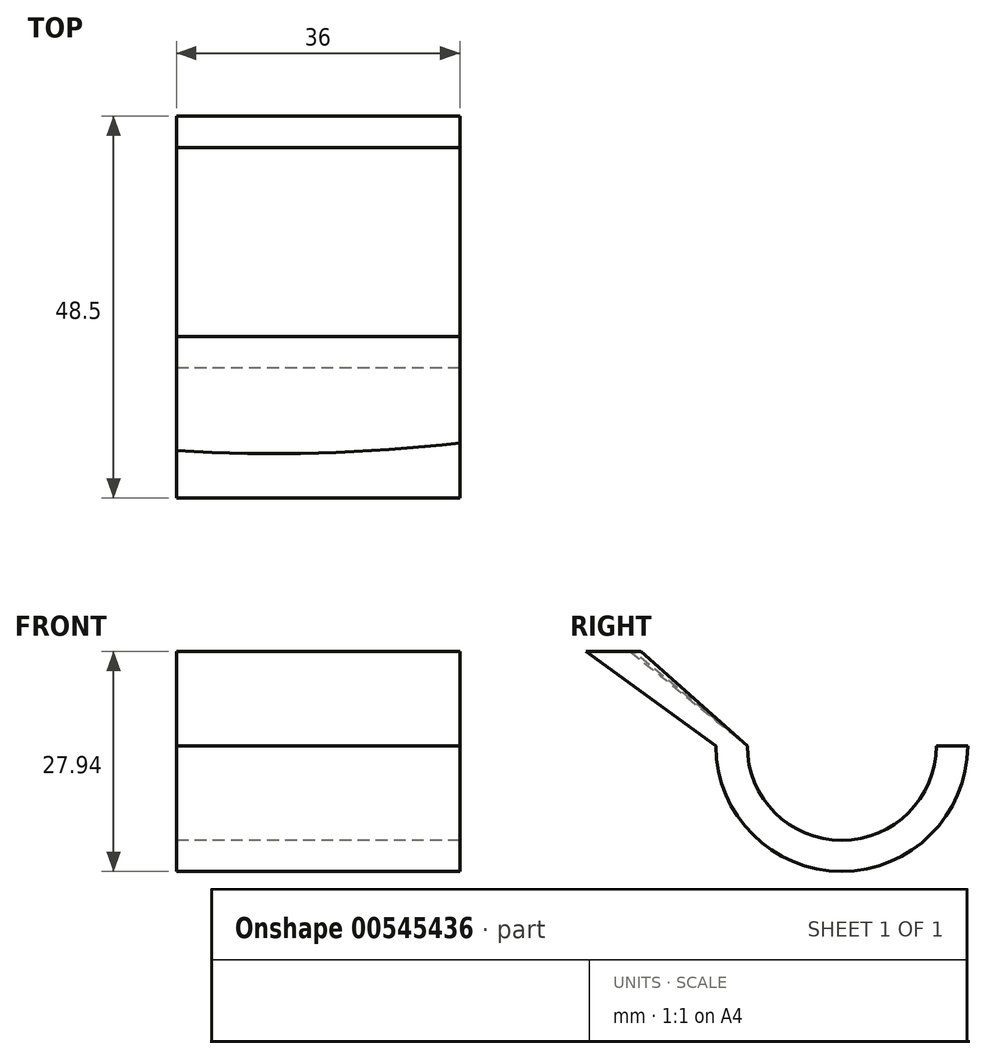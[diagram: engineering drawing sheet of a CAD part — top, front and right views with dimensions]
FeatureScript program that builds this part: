
annotation { "Feature Type Name" : "Feature", "Feature Type Description" : "" }
export const myFeature = defineFeature(function(context is Context, id is Id, definition is map)
    precondition{}
    {
        {
            var Q0;
            Q0=qCreatedBy(makeId("Right.planeOp"),FACE);
            var sketch = newSketch(context, id + "F0", { "sketchPlane" : qUnion([Q0])});
            skArc(sketch, "E0", {"start": v(-12, 0) * mm, "mid": v(0, -12) * mm, "end": v(12, 0) * mm});
            skLineSegment(sketch, "E1", {"start": v(12, 0) * mm, "end": v(16, 0) * mm});
            skLineSegment(sketch, "E2", {"start": v(-12, 0) * mm, "end": v(-16, 0) * mm});
            skArc(sketch, "E3", {"start": v(-16, 0) * mm, "mid": v(0, -15.94) * mm, "end": v(16, 0) * mm});
            skSolve(sketch);
        }
        {
            var Q0;
            Q0=qCreatedBy(makeId("Top.planeOp"),FACE);
            var sketch = newSketch(context, id + "F1", { "sketchPlane" : qUnion([Q0])});
            skLineSegment(sketch, "E4", {"start": v(0, 0) * mm, "end": v(-36, 0) * mm});
            skSolve(sketch);
        }
        {
            var Q0;
            Q0 = qSketchRegion(id + "F0", true);
            var Q1;
            Q1=sQuery(id+"F1.wireOp",EDGE,"E4");
            sweep(context, id + "F2", {"profiles" : qUnion([Q0]), "path" : qUnion([Q1])});
        }
        {
            var Q0;
            Q0=qCreatedBy(makeId("Top.planeOp"),FACE);
            cPlane(context, id + "F3", {"entities" : qUnion([Q0]), "cplaneType" : CPlaneType.OFFSET, "offset" : 12 * mm, "width" : 150 * mm, "height" : 150 * mm});
        }
        {
            var Q0;
            Q0=qCreatedBy(id+"F3.planeOp",FACE);
            var sketch = newSketch(context, id + "F4", { "sketchPlane" : qUnion([Q0])});
            skArc(sketch, "E5", {"start": v(-36, -26.5) * mm, "mid": v(-17.98, -26.8) * mm, "end": v(0, -25.5) * mm});
            skLineSegment(sketch, "E6", {"start": v(-36, -26.5) * mm, "end": v(-36, -32.5) * mm});
            skLineSegment(sketch, "E7", {"start": v(-36, -32.5) * mm, "end": v(0, -32.5) * mm});
            skLineSegment(sketch, "E8", {"start": v(0, -32.5) * mm, "end": v(0, -25.5) * mm});
            skSolve(sketch);
        }
        {
            var Q1;
            Q1=makeQuery(id+"F2.opSweep","SWEPT_FACE",FACE,{"disambiguationData":[OSD([sQuery(id+"F0.wireOp",EDGE,"E2"),sQuery(id+"F1.wireOp",EDGE,"E4")])]});
            var Q2;
            Q2=makeQuery(id+"F4.imprint","IMPRINT",FACE,{"disambiguationData":[TD([[makeQuery(id+"F4.imprint","IMPRINT",EDGE,{"derivedFrom":sQuery(id+"F4.wireOp",EDGE,"E5")}),-1.0]])]});
            loft(context, id + "F5", {"operationType" : NewBodyOperationType.ADD, "sheetProfilesArray" : [{ "sheetProfileEntities" : qUnion([Q1]) }, { "sheetProfileEntities" : qUnion([Q2]) }]});
        }
    });
